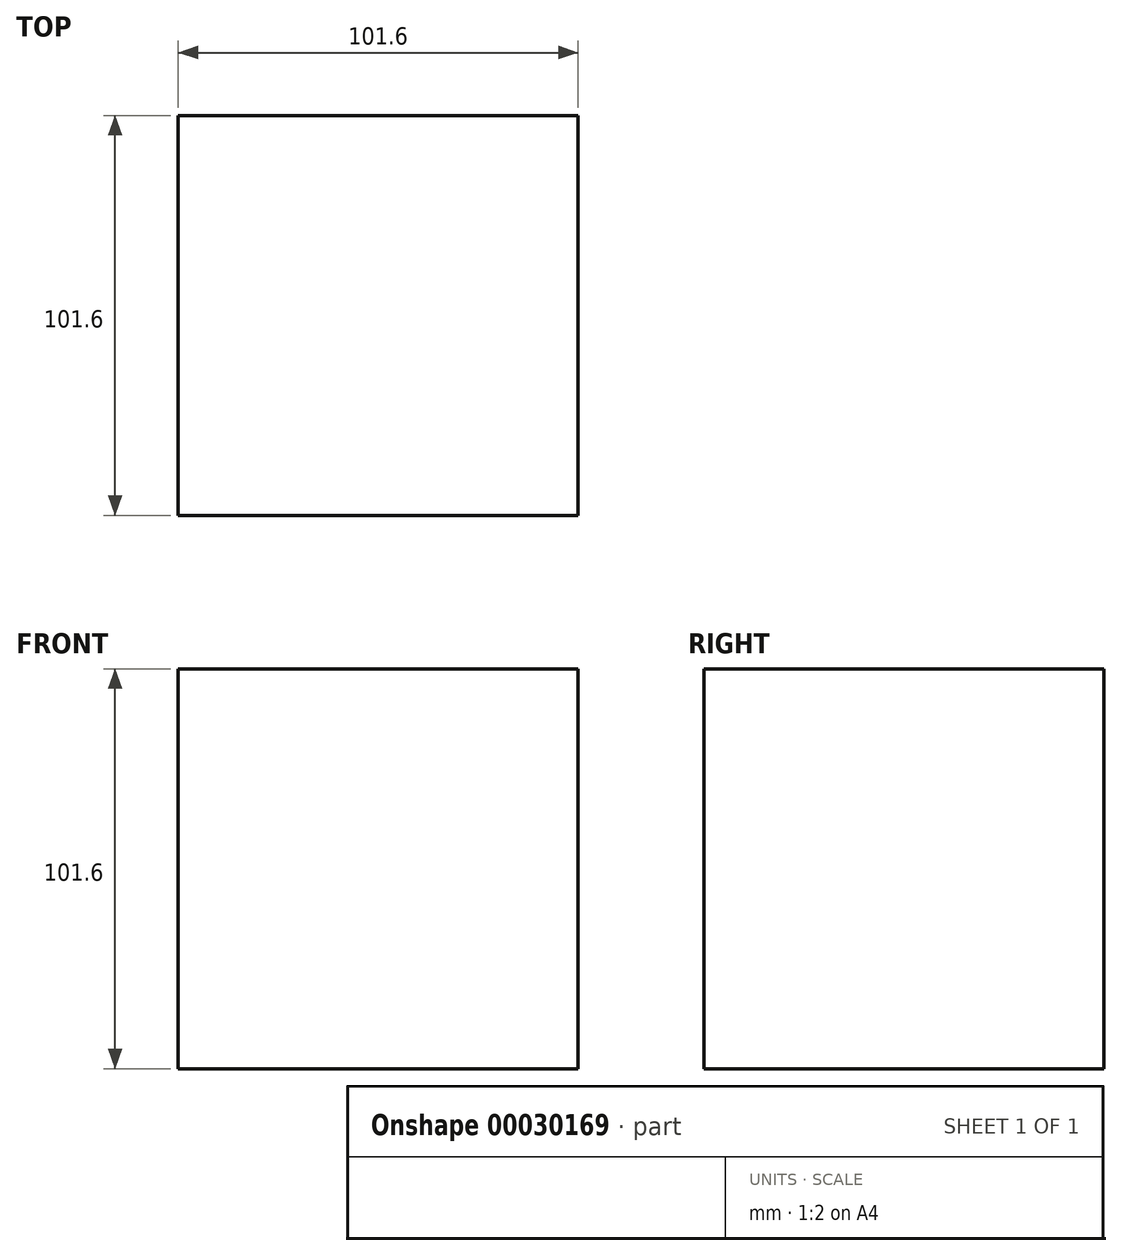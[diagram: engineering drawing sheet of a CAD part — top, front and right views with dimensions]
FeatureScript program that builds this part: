
annotation { "Feature Type Name" : "Feature", "Feature Type Description" : "" }
export const myFeature = defineFeature(function(context is Context, id is Id, definition is map)
    precondition{}
    {
        {
            var Q0;
            Q0=qCreatedBy(makeId("Front.planeOp"),FACE);
            var sketch = newSketch(context, id + "F0", { "sketchPlane" : qUnion([Q0])});
            skLineSegment(sketch, "E0.bottom", {"start": v(-47.34, 52.58) * mm, "end": v(54.26, 52.58) * mm});
            skLineSegment(sketch, "E0.top", {"start": v(-47.34, -49.02) * mm, "end": v(54.26, -49.02) * mm});
            skLineSegment(sketch, "E0.left", {"start": v(-47.34, 52.58) * mm, "end": v(-47.34, -49.02) * mm});
            skLineSegment(sketch, "E0.right", {"start": v(54.26, 52.58) * mm, "end": v(54.26, -49.02) * mm});
            skSolve(sketch);
        }
        {
            var Q0;
            Q0 = qSketchRegion(id + "F0", true);
            extrude(context, id + "F1", {"entities" : qUnion([Q0]), "depth" : 101.6 * mm});
        }
    });
